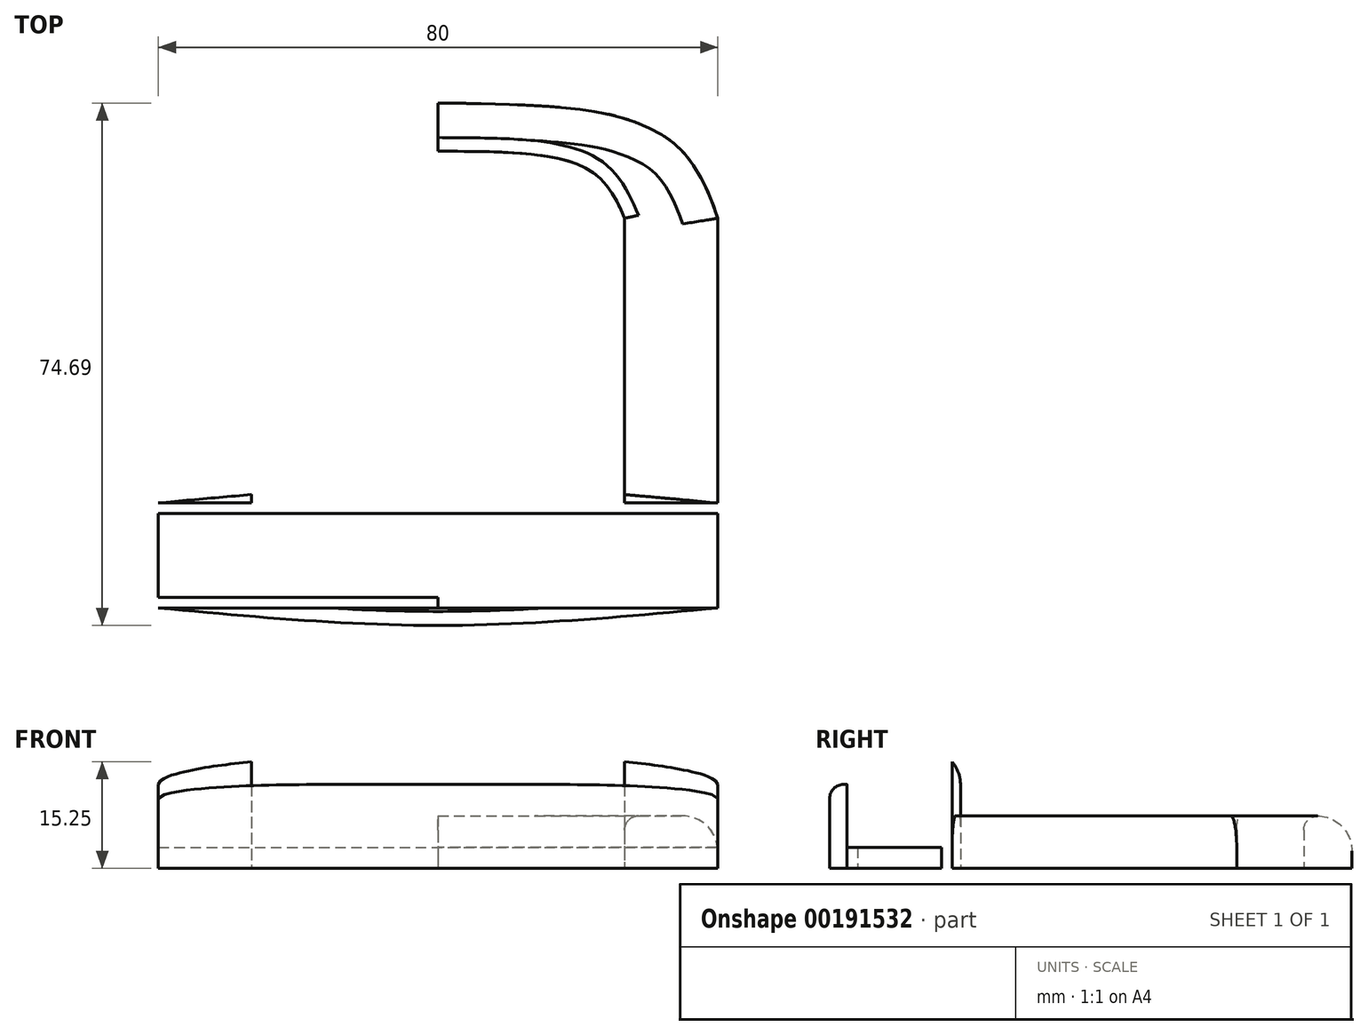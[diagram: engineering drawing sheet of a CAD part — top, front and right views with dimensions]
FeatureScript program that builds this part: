
annotation { "Feature Type Name" : "Feature", "Feature Type Description" : "" }
export const myFeature = defineFeature(function(context is Context, id is Id, definition is map)
    precondition{}
    {
        {
            var Q0;
            Q0=qCreatedBy(makeId("Top.planeOp"),FACE);
            var sketch = newSketch(context, id + "F0", { "sketchPlane" : qUnion([Q0])});
            skLineSegment(sketch, "E0", {"start": v(-40, 0) * mm, "end": v(0, 0) * mm});
            skLineSegment(sketch, "E1", {"start": v(-40, 0) * mm, "end": v(-40, 7.5) * mm});
            skLineSegment(sketch, "E2.MirrorCS", {"start": v(-40, 0) * mm, "end": v(-40, -7.5) * mm});
            skLineSegment(sketch, "E3.MirrorCS", {"start": v(40, 0) * mm, "end": v(40, 7.5) * mm});
            skLineSegment(sketch, "E4.MirrorCS", {"start": v(40, 0) * mm, "end": v(40, -7.5) * mm});
            skLineSegment(sketch, "E5.MirrorCS", {"start": v(40, 0) * mm, "end": v(0, 0) * mm});
            skLineSegment(sketch, "E6", {"start": v(0, 0) * mm, "end": v(0, 10) * mm});
            skFitSpline(sketch, "E7", {"points": [v(-40, 7.5) * mm, v(0, 10) * mm, v(40, 7.5) * mm], "startDerivative": vector(80, 7.5) * mm, "endDerivative": vector(80, -7.5) * mm});
            skFitSpline(sketch, "E8.MirrorCS", {"points": [v(-40, -7.5) * mm, v(0, -10) * mm, v(40, -7.5) * mm], "startDerivative": vector(80, -7.5) * mm, "endDerivative": vector(80, 7.5) * mm});
            skLineSegment(sketch, "E9", {"start": v(-40, 7.5) * mm, "end": v(40, 7.5) * mm});
            skLineSegment(sketch, "E10", {"start": v(40, -7.5) * mm, "end": v(-40, -7.5) * mm});
            skLineSegment(sketch, "E11", {"start": v(0, 0) * mm, "end": v(0, 64.7) * mm, "construction": true});
            skLineSegment(sketch, "E12.bottom", {"start": v(-40, 7.5) * mm, "end": v(-40, 7.5) * mm});
            skLineSegment(sketch, "E12.top", {"start": v(-40, 48.22) * mm, "end": v(-40, 48.22) * mm});
            skLineSegment(sketch, "E12.left", {"start": v(-40, 7.5) * mm, "end": v(-40, 48.22) * mm});
            skLineSegment(sketch, "E12.right", {"start": v(-40, 7.5) * mm, "end": v(-40, 48.22) * mm});
            skFitSpline(sketch, "E13", {"points": [v(-40, 48.22) * mm, v(-29.81, 61.28) * mm, v(0, 64.7) * mm], "startDerivative": vector(20.68, 63.03) * mm, "endDerivative": vector(100.12, 0.76) * mm});
            skFitSpline(sketch, "E14.MirrorCS", {"points": [v(40, 48.22) * mm, v(29.81, 61.28) * mm, v(0, 64.7) * mm], "startDerivative": vector(-20.68, 63.03) * mm, "endDerivative": vector(-100.12, 0.76) * mm});
            skLineSegment(sketch, "E15.MirrorCS", {"start": v(40, 7.5) * mm, "end": v(40, 48.22) * mm});
            skLineSegment(sketch, "E16", {"start": v(-26.67, 8.75) * mm, "end": v(-26.67, 48.22) * mm});
            skFitSpline(sketch, "E17", {"points": [v(-26.67, 48.22) * mm, v(-21.54, 55.19) * mm, v(0, 57.8) * mm], "startDerivative": vector(9, 20.66) * mm, "endDerivative": vector(41.85, 0.05) * mm});
            skFitSpline(sketch, "E18.MirrorCS", {"points": [v(26.67, 48.22) * mm, v(21.54, 55.19) * mm, v(0, 57.8) * mm], "startDerivative": vector(-9, 20.66) * mm, "endDerivative": vector(-41.85, 0.05) * mm});
            skLineSegment(sketch, "E19.MirrorCS", {"start": v(26.67, 8.75) * mm, "end": v(26.67, 48.22) * mm});
            skLineSegment(sketch, "E20", {"start": v(0, 64.7) * mm, "end": v(0, 57.8) * mm});
            skLineSegment(sketch, "E21", {"start": v(26.67, 8.75) * mm, "end": v(26.67, 7.5) * mm});
            skLineSegment(sketch, "E22", {"start": v(-26.67, 8.75) * mm, "end": v(-26.67, 7.5) * mm});
            skLineSegment(sketch, "E23", {"start": v(-40, 7.5) * mm, "end": v(-40, 6) * mm});
            skLineSegment(sketch, "E24.MirrorCS", {"start": v(-40, -7.5) * mm, "end": v(-40, -6) * mm});
            skLineSegment(sketch, "E25.MirrorCS", {"start": v(40, -7.5) * mm, "end": v(40, -6) * mm});
            skLineSegment(sketch, "E26.MirrorCS", {"start": v(40, 7.5) * mm, "end": v(40, 6) * mm});
            skLineSegment(sketch, "E27", {"start": v(-40, 6) * mm, "end": v(40, 6) * mm});
            skLineSegment(sketch, "E28", {"start": v(-40, -6) * mm, "end": v(40, -6) * mm});
            skLineSegment(sketch, "E29", {"start": v(0, 10) * mm, "end": v(0, -10) * mm});
            skSolve(sketch);
        }
        {
            var Q0;
            Q0=makeQuery(id+"F0.imprint","IMPRINT",FACE,{"disambiguationData":[TD([[makeQuery(id+"F0.imprint","IMPRINT",EDGE,{"derivedFrom":sQuery(id+"F0.wireOp",EDGE,"E14.MirrorCS")}),1.0]])]});
            var Q1;
            {var subQ0=sQuery(id+"F0.wireOp",EDGE,"E12.right");Q1=makeQuery(id+"F0.imprint","IMPRINT",FACE,{"disambiguationData":[TD([[makeQuery(id+"F0.imprint","IMPRINT",EDGE,{"derivedFrom":subQ0}),-1.0]])]});}
            var Q2;
            Q2=makeQuery(id+"F0.imprint","IMPRINT",FACE,{"disambiguationData":[TD([[makeQuery(id+"F0.imprint","IMPRINT",EDGE,{"derivedFrom":sQuery(id+"F0.wireOp",EDGE,"E14.MirrorCS")}),1.0]])]});
            extrude(context, id + "F1", {"entities" : qUnion([Q0, Q1, Q2]), "depth" : 7.5 * mm});
        }
        {
            var Q0;
            {var subQ0=sQuery(id+"F0.wireOp",EDGE,"E29");var subQ1=sQuery(id+"F0.wireOp",EDGE,"E7");var subQ2=makeQuery(id+"F0.imprint","INTERSECT",VERTEX,{"derivedFrom":[subQ1,subQ0]});Q0=makeQuery(id+"F0.imprint","IMPRINT",FACE,{"disambiguationData":[TD([[makeQuery(id+"F0.imprint","IMPRINT",EDGE,{"disambiguationData":[TD([[subQ2,1.0]])],"derivedFrom":subQ1}),-1.0]])]});}
            var Q1;
            {var subQ0=sQuery(id+"F0.wireOp",EDGE,"E29");var subQ1=sQuery(id+"F0.wireOp",EDGE,"E7");var subQ2=makeQuery(id+"F0.imprint","INTERSECT",VERTEX,{"derivedFrom":[subQ1,subQ0]});Q1=makeQuery(id+"F0.imprint","IMPRINT",FACE,{"disambiguationData":[TD([[makeQuery(id+"F0.imprint","IMPRINT",EDGE,{"disambiguationData":[TD([[subQ2,-1.0]])],"derivedFrom":subQ1}),-1.0]])]});}
            var Q2;
            {var subQ1=sQuery(id+"F0.wireOp",EDGE,"E26.MirrorCS");Q2=makeQuery(id+"F0.imprint","IMPRINT",FACE,{"disambiguationData":[TD([[makeQuery(id+"F0.imprint","IMPRINT",EDGE,{"derivedFrom":subQ1}),-1.0]])]});}
            var Q3;
            {var subQ1=sQuery(id+"F0.wireOp",EDGE,"E23");Q3=makeQuery(id+"F0.imprint","IMPRINT",FACE,{"disambiguationData":[TD([[makeQuery(id+"F0.imprint","IMPRINT",EDGE,{"derivedFrom":subQ1}),1.0]])]});}
            var Q4;
            {var subQ0=sQuery(id+"F0.wireOp",EDGE,"E9");var subQ3=sQuery(id+"F0.wireOp",EDGE,"E22");var subQ5=makeQuery(id+"F0.imprint","INTERSECT",VERTEX,{"derivedFrom":[subQ0,subQ3]});Q4=makeQuery(id+"F0.imprint","IMPRINT",FACE,{"disambiguationData":[TD([[makeQuery(id+"F0.imprint","IMPRINT",EDGE,{"disambiguationData":[TD([[subQ5,1.0]])],"derivedFrom":subQ3}),-1.0]])]});}
            var Q5;
            {var subQ0=sQuery(id+"F0.wireOp",EDGE,"E9");var subQ3=sQuery(id+"F0.wireOp",EDGE,"E21");var subQ5=makeQuery(id+"F0.imprint","INTERSECT",VERTEX,{"derivedFrom":[subQ0,subQ3]});Q5=makeQuery(id+"F0.imprint","IMPRINT",FACE,{"disambiguationData":[TD([[makeQuery(id+"F0.imprint","IMPRINT",EDGE,{"disambiguationData":[TD([[subQ5,1.0]])],"derivedFrom":subQ3}),1.0]])]});}
            extrude(context, id + "F2", {"entities" : qUnion([Q0, Q1, Q2, Q3, Q4, Q5]), "operationType" : NewBodyOperationType.ADD, "depth" : 17 * mm});
        }
        {
            var Q0;
            {var subQ0=sQuery(id+"F0.wireOp",EDGE,"E0");Q0=makeQuery(id+"F0.imprint","IMPRINT",FACE,{"disambiguationData":[TD([[makeQuery(id+"F0.imprint","IMPRINT",EDGE,{"derivedFrom":subQ0}),1.0]])]});}
            var Q1;
            {var subQ0=sQuery(id+"F0.wireOp",EDGE,"E0");Q1=makeQuery(id+"F0.imprint","IMPRINT",FACE,{"disambiguationData":[TD([[makeQuery(id+"F0.imprint","IMPRINT",EDGE,{"derivedFrom":subQ0}),-1.0]])]});}
            var Q2;
            {var subQ0=sQuery(id+"F0.wireOp",EDGE,"E3.MirrorCS");Q2=makeQuery(id+"F0.imprint","IMPRINT",FACE,{"disambiguationData":[TD([[makeQuery(id+"F0.imprint","IMPRINT",EDGE,{"derivedFrom":subQ0}),1.0]])]});}
            var Q3;
            {var subQ0=sQuery(id+"F0.wireOp",EDGE,"E4.MirrorCS");Q3=makeQuery(id+"F0.imprint","IMPRINT",FACE,{"disambiguationData":[TD([[makeQuery(id+"F0.imprint","IMPRINT",EDGE,{"derivedFrom":subQ0}),-1.0]])]});}
            extrude(context, id + "F3", {"entities" : qUnion([Q0, Q1, Q2, Q3]), "depth" : 3 * mm});
        }
        {
            var Q0;
            Q0=makeQuery(id+"F1.opExtrude","CAP_EDGE",EDGE,{"disambiguationData":[OSD([sQuery(id+"F0.wireOp",EDGE,"E15.MirrorCS")])],"isStart":false});
            var Q1;
            Q1=makeQuery(id+"F1.opExtrude","CAP_EDGE",EDGE,{"disambiguationData":[OSD([sQuery(id+"F0.wireOp",EDGE,"E14.MirrorCS")])],"isStart":false});
            var Q2;
            Q2=makeQuery(id+"F1.opExtrude","CAP_EDGE",EDGE,{"disambiguationData":[OSD([sQuery(id+"F0.wireOp",EDGE,"E12.right")])],"isStart":false});
            var Q3;
            Q3=makeQuery(id+"F1.opExtrude","CAP_EDGE",EDGE,{"disambiguationData":[OSD([sQuery(id+"F0.wireOp",EDGE,"E13")])],"isStart":false});
            fillet(context, id + "F4", {"entities" : qUnion([Q0, Q1, Q2, Q3]), "radius" : 5 * mm, "tangentPropagation" : true, "allowEdgeOverflow" : false});
        }
        {
            var Q0;
            Q0=makeQuery(id+"F2.opExtrude","CAP_EDGE",EDGE,{"disambiguationData":[OSD([sQuery(id+"F0.wireOp",EDGE,"E7")])],"isStart":false});
            var Q1;
            Q1=makeQuery(id+"F2.opExtrude","CAP_EDGE",EDGE,{"disambiguationData":[OSD([sQuery(id+"F0.wireOp",EDGE,"E8.MirrorCS")])],"isStart":false});
            fillet(context, id + "F5", {"entities" : qUnion([Q0, Q1]), "radius" : 5 * mm, "tangentPropagation" : true, "allowEdgeOverflow" : false});
        }
        {
            var Q0;
            Q0=makeQuery(id+"F1.opExtrude","CAP_EDGE",EDGE,{"disambiguationData":[OSD([sQuery(id+"F0.wireOp",EDGE,"E16"),sQuery(id+"F0.wireOp",EDGE,"E22")])],"isStart":false});
            var Q1;
            Q1=makeQuery(id+"F1.opExtrude","CAP_EDGE",EDGE,{"disambiguationData":[OSD([sQuery(id+"F0.wireOp",EDGE,"E17")])],"isStart":false});
            var Q2;
            Q2=makeQuery(id+"F1.opExtrude","CAP_EDGE",EDGE,{"disambiguationData":[OSD([sQuery(id+"F0.wireOp",EDGE,"E18.MirrorCS")])],"isStart":false});
            var Q3;
            Q3=makeQuery(id+"F1.opExtrude","CAP_EDGE",EDGE,{"disambiguationData":[OSD([sQuery(id+"F0.wireOp",EDGE,"E19.MirrorCS"),sQuery(id+"F0.wireOp",EDGE,"E21")])],"isStart":false});
            fillet(context, id + "F6", {"entities" : qUnion([Q0, Q1, Q2, Q3]), "radius" : 2 * mm, "tangentPropagation" : true, "allowEdgeOverflow" : false});
        }
        {
            var Q0;
            {var subQ1=sQuery(id+"F0.wireOp",EDGE,"E8.MirrorCS");var subQ3=sQuery(id+"F0.wireOp",EDGE,"E29");var subQ4=makeQuery(id+"F0.imprint","INTERSECT",VERTEX,{"derivedFrom":[subQ1,subQ3]});Q0=makeQuery(id+"F0.imprint","IMPRINT",FACE,{"disambiguationData":[TD([[makeQuery(id+"F0.imprint","IMPRINT",EDGE,{"disambiguationData":[TD([[subQ4,1.0]])],"derivedFrom":subQ3}),-1.0]])]});}
            var Q1;
            {var subQ0=sQuery(id+"F0.wireOp",EDGE,"E24.MirrorCS");Q1=makeQuery(id+"F0.imprint","IMPRINT",FACE,{"disambiguationData":[TD([[makeQuery(id+"F0.imprint","IMPRINT",EDGE,{"derivedFrom":subQ0}),-1.0]])]});}
            var Q2;
            {var subQ0=sQuery(id+"F0.wireOp",EDGE,"E25.MirrorCS");Q2=makeQuery(id+"F0.imprint","IMPRINT",FACE,{"disambiguationData":[TD([[makeQuery(id+"F0.imprint","IMPRINT",EDGE,{"derivedFrom":subQ0}),1.0]])]});}
            var Q3;
            {var subQ1=sQuery(id+"F0.wireOp",EDGE,"E8.MirrorCS");var subQ3=sQuery(id+"F0.wireOp",EDGE,"E29");var subQ4=makeQuery(id+"F0.imprint","INTERSECT",VERTEX,{"derivedFrom":[subQ1,subQ3]});Q3=makeQuery(id+"F0.imprint","IMPRINT",FACE,{"disambiguationData":[TD([[makeQuery(id+"F0.imprint","IMPRINT",EDGE,{"disambiguationData":[TD([[subQ4,1.0]])],"derivedFrom":subQ3}),1.0]])]});}
            extrude(context, id + "F7", {"entities" : qUnion([Q0, Q1, Q2, Q3]), "operationType" : NewBodyOperationType.ADD, "depth" : 12 * mm});
        }
        {
            var Q0;
            Q0=makeQuery(id+"F7.opExtrude","CAP_EDGE",EDGE,{"disambiguationData":[OSD([sQuery(id+"F0.wireOp",EDGE,"E8.MirrorCS")])],"isStart":false});
            fillet(context, id + "F8", {"entities" : qUnion([Q0]), "radius" : 2 * mm, "tangentPropagation" : true, "allowEdgeOverflow" : false});
        }
    });
